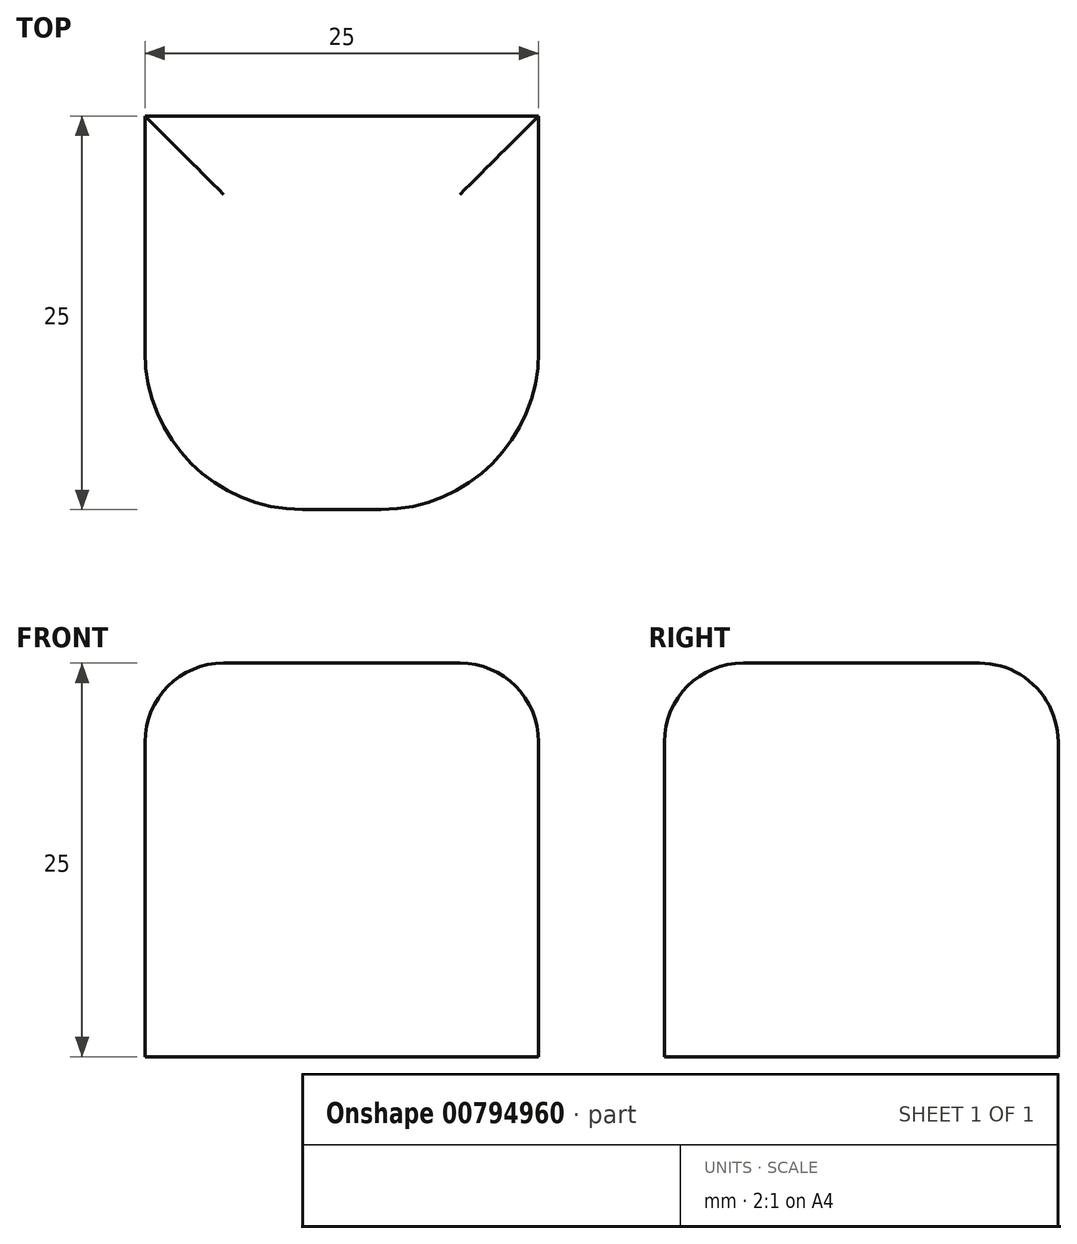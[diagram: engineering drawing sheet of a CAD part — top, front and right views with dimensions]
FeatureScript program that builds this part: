
annotation { "Feature Type Name" : "Feature", "Feature Type Description" : "" }
export const myFeature = defineFeature(function(context is Context, id is Id, definition is map)
    precondition{}
    {
        {
            var Q0;
            Q0=qCreatedBy(makeId("Top.planeOp"),FACE);
            var sketch = newSketch(context, id + "F0", { "sketchPlane" : qUnion([Q0])});
            skLineSegment(sketch, "E0.bottom", {"start": v(-12.5, 12.5) * mm, "end": v(12.5, 12.5) * mm});
            skLineSegment(sketch, "E0.top", {"start": v(-12.5, -12.5) * mm, "end": v(12.5, -12.5) * mm});
            skLineSegment(sketch, "E0.left", {"start": v(-12.5, 12.5) * mm, "end": v(-12.5, -12.5) * mm});
            skLineSegment(sketch, "E0.right", {"start": v(12.5, 12.5) * mm, "end": v(12.5, -12.5) * mm});
            skLineSegment(sketch, "E1", {"start": v(-12.5, 12.5) * mm, "end": v(12.5, -12.5) * mm, "construction": true});
            skSolve(sketch);
        }
        {
            var Q0;
            Q0=makeQuery(id+"F0.imprint","IMPRINT",FACE,{"disambiguationData":[TD([[makeQuery(id+"F0.imprint","IMPRINT",EDGE,{"derivedFrom":sQuery(id+"F0.wireOp",EDGE,"E0.bottom")}),-1.0]])]});
            extrude(context, id + "F1", {"entities" : qUnion([Q0]), "depth" : 25 * mm, "offsetDistance" : 25 * mm});
        }
        {
            var Q0;
            Q0=makeQuery(id+"F1.opExtrude","CAP_FACE",FACE,{"disambiguationData":[OSD([sQuery(id+"F0.wireOp",EDGE,"E0.bottom"),sQuery(id+"F0.wireOp",EDGE,"E0.top"),sQuery(id+"F0.wireOp",EDGE,"E0.left"),sQuery(id+"F0.wireOp",EDGE,"E0.right")])],"isStart":false});
            fillet(context, id + "F2", {"entities" : qUnion([Q0]), "radius" : 5 * mm, "tangentPropagation" : true, "allowEdgeOverflow" : false});
        }
        {
            var Q0;
            Q0=makeQuery(id+"F1.opExtrude","SWEPT_EDGE",EDGE,{"disambiguationData":[OSD([sQuery(id+"F0.wireOp",EDGE,"E0.top"),sQuery(id+"F0.wireOp",EDGE,"E0.right")])]});
            var Q1;
            Q1=makeQuery(id+"F1.opExtrude","SWEPT_EDGE",EDGE,{"disambiguationData":[OSD([sQuery(id+"F0.wireOp",EDGE,"E0.top"),sQuery(id+"F0.wireOp",EDGE,"E0.left")])]});
            fillet(context, id + "F3", {"entities" : qUnion([Q0, Q1]), "radius" : 10 * mm, "tangentPropagation" : true, "allowEdgeOverflow" : false});
        }
    });
